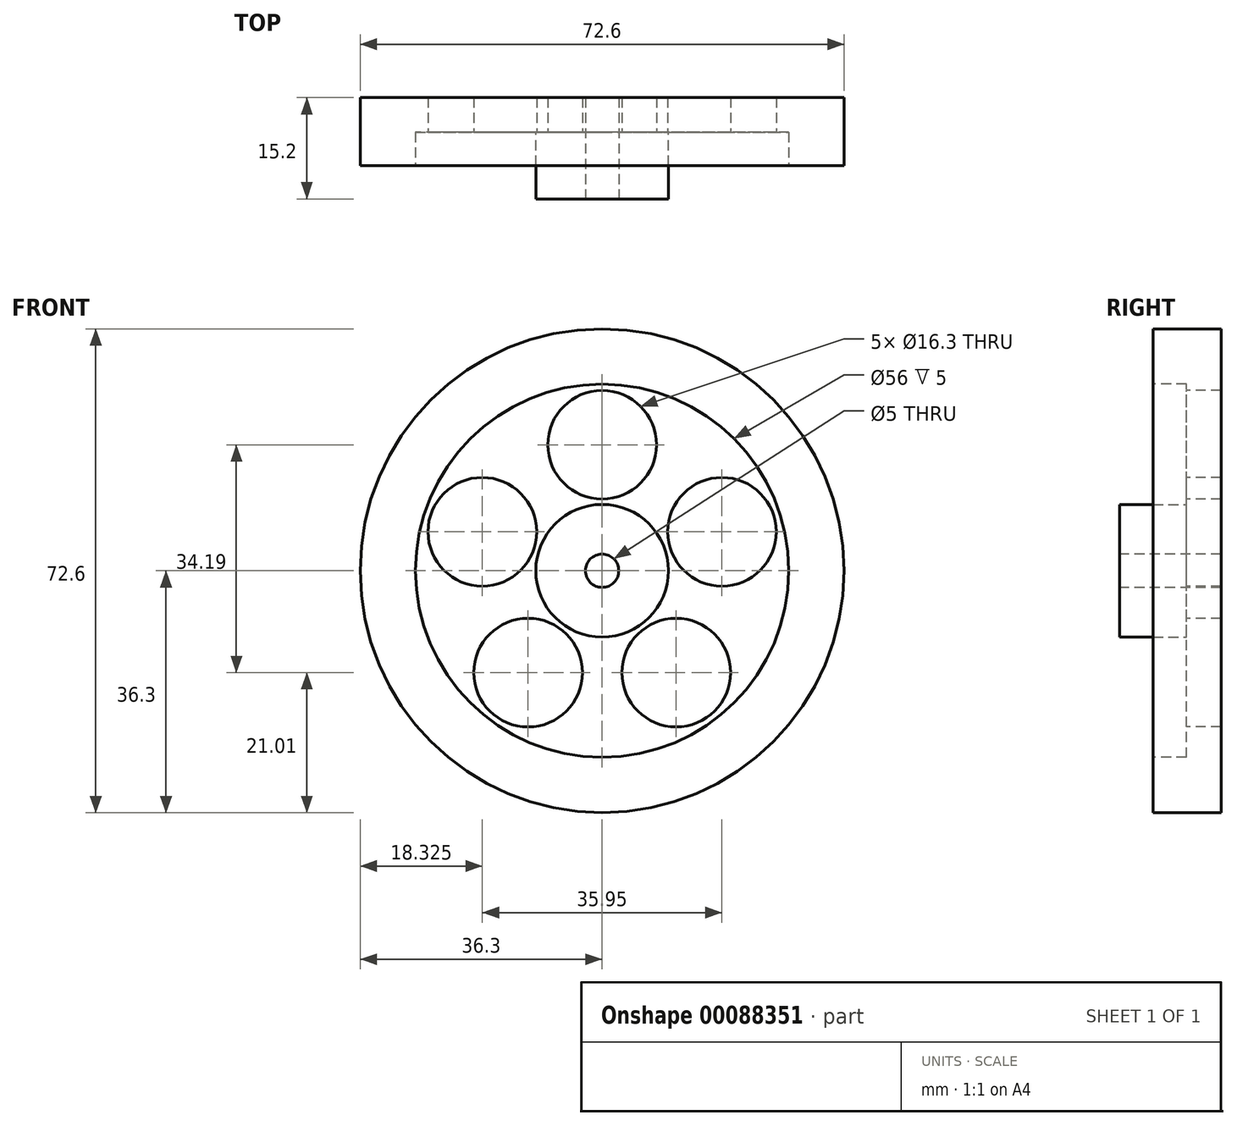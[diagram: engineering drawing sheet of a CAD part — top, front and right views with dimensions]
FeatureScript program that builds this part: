
annotation { "Feature Type Name" : "Feature", "Feature Type Description" : "" }
export const myFeature = defineFeature(function(context is Context, id is Id, definition is map)
    precondition{}
    {
        {
            var Q0;
            Q0=qCreatedBy(makeId("Front.planeOp"),FACE);
            var sketch = newSketch(context, id + "F0", { "sketchPlane" : qUnion([Q0])});
            skCircle(sketch, "E0", {"center": v(0, 0) * mm, "radius": 36.3 * mm});
            skSolve(sketch);
        }
        {
            var Q0;
            Q0 = qSketchRegion(id + "F0", true);
            extrude(context, id + "F1", {"entities" : qUnion([Q0]), "depth" : 10.2 * mm});
        }
        {
            var Q0;
            Q0=makeQuery(id+"F1.opExtrude","CAP_FACE",FACE,{"disambiguationData":[OSD([sQuery(id+"F0.wireOp",EDGE,"E0")])],"isStart":false});
            var sketch = newSketch(context, id + "F2", { "sketchPlane" : qUnion([Q0])});
            skCircle(sketch, "E1", {"center": v(0, 0) * mm, "radius": 28 * mm});
            skSolve(sketch);
        }
        {
            var Q0;
            Q0 = qSketchRegion(id + "F2", true);
            extrude(context, id + "F3", {"entities" : qUnion([Q0]), "operationType" : NewBodyOperationType.REMOVE, "oppositeDirection" : true, "depth" : 5 * mm});
        }
        {
            var Q0;
            Q0=makeQuery(id+"F3.boolean.opBoolean","COPY",FACE,{"derivedFrom":makeQuery(id+"F3.opExtrude","CAP_FACE",FACE,{"disambiguationData":[OSD([sQuery(id+"F2.wireOp",EDGE,"E1")])],"isStart":false})});
            var sketch = newSketch(context, id + "F4", { "sketchPlane" : qUnion([Q0])});
            skCircle(sketch, "E2", {"center": v(0, 0) * mm, "radius": 9.95 * mm});
            skSolve(sketch);
        }
        {
            var Q0;
            Q0 = qSketchRegion(id + "F4", true);
            extrude(context, id + "F5", {"entities" : qUnion([Q0]), "operationType" : NewBodyOperationType.ADD, "depth" : 10 * mm});
        }
        {
            var Q0;
            Q0=makeQuery(id+"F5.opExtrude","CAP_FACE",FACE,{"disambiguationData":[OSD([sQuery(id+"F4.wireOp",EDGE,"E2")])],"isStart":false});
            var sketch = newSketch(context, id + "F6", { "sketchPlane" : qUnion([Q0])});
            skCircle(sketch, "E3", {"center": v(0, 0) * mm, "radius": 2.5 * mm});
            skSolve(sketch);
        }
        {
            var Q0;
            Q0 = qSketchRegion(id + "F6", true);
            extrude(context, id + "F7", {"entities" : qUnion([Q0]), "operationType" : NewBodyOperationType.REMOVE, "endBound" : BoundingType.THROUGH_ALL, "oppositeDirection" : true, "depth" : 25 * mm});
        }
        {
            var Q0;
            Q0=makeQuery(id+"F3.boolean.opBoolean","COPY",FACE,{"derivedFrom":makeQuery(id+"F3.opExtrude","CAP_FACE",FACE,{"disambiguationData":[OSD([sQuery(id+"F2.wireOp",EDGE,"E1")])],"isStart":false})});
            var sketch = newSketch(context, id + "F8", { "sketchPlane" : qUnion([Q0])});
            skCircle(sketch, "E4", {"center": v(0, 18.9) * mm, "radius": 8.15 * mm});
            skCircle(sketch, "E5.1.0", {"center": v(-17.97, 5.84) * mm, "radius": 8.15 * mm});
            skCircle(sketch, "E5.2.0", {"center": v(-11.1, -15.3) * mm, "radius": 8.15 * mm});
            skCircle(sketch, "E5.3.0", {"center": v(11.1, -15.3) * mm, "radius": 8.15 * mm});
            skCircle(sketch, "E5.4.0", {"center": v(17.97, 5.84) * mm, "radius": 8.15 * mm});
            skPoint(sketch, "E5.center", {"position": v(0, 0) * mm});
            skSolve(sketch);
        }
        {
            var Q0;
            Q0 = qSketchRegion(id + "F8", true);
            extrude(context, id + "F9", {"entities" : qUnion([Q0]), "operationType" : NewBodyOperationType.REMOVE, "endBound" : BoundingType.THROUGH_ALL, "oppositeDirection" : true, "depth" : 25 * mm});
        }
    });
